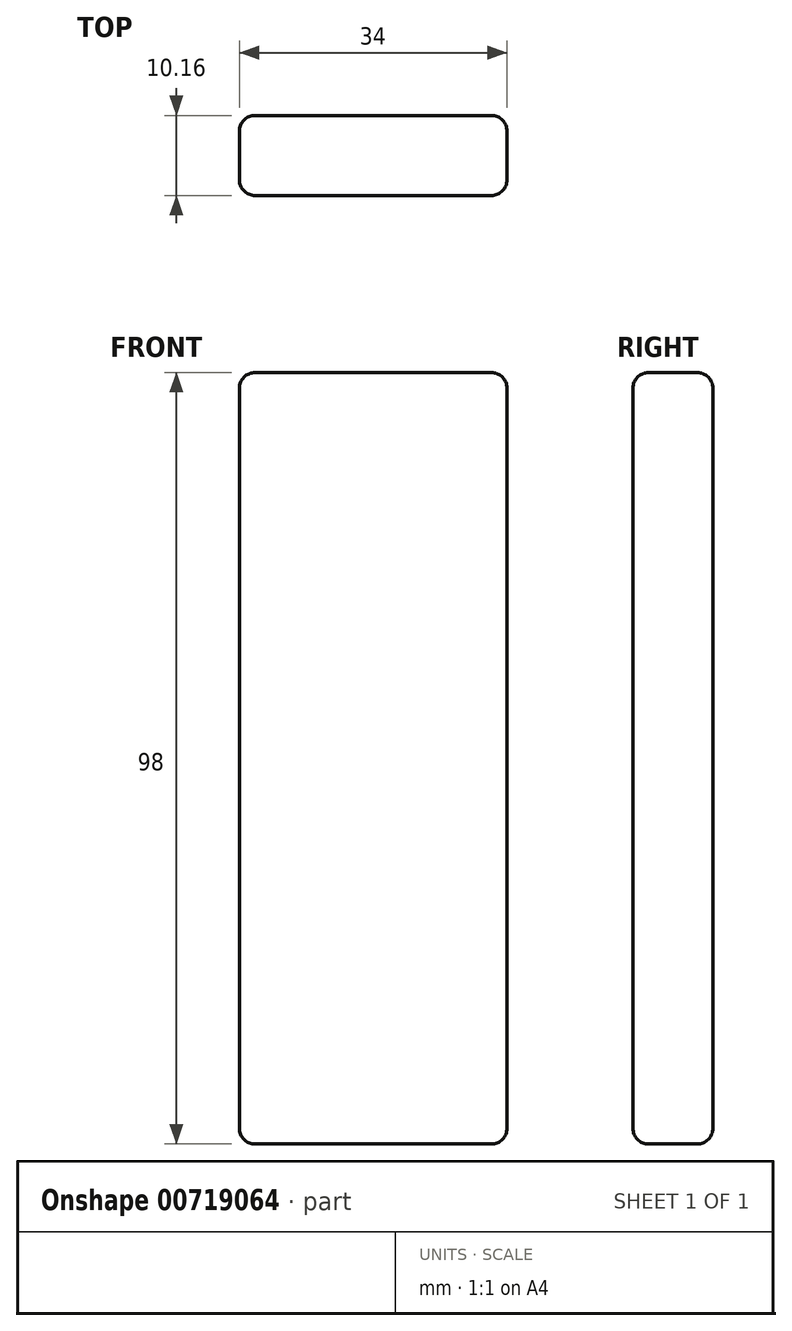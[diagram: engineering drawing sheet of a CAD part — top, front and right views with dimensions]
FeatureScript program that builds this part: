
annotation { "Feature Type Name" : "Feature", "Feature Type Description" : "" }
export const myFeature = defineFeature(function(context is Context, id is Id, definition is map)
    precondition{}
    {
        {
            var Q0;
            Q0=qCreatedBy(makeId("Front.planeOp"),FACE);
            var sketch = newSketch(context, id + "F0", { "sketchPlane" : qUnion([Q0])});
            skLineSegment(sketch, "E0.bottom", {"start": v(-17, 55.23) * mm, "end": v(17, 55.23) * mm});
            skLineSegment(sketch, "E0.top", {"start": v(-17, -42.77) * mm, "end": v(17, -42.77) * mm});
            skLineSegment(sketch, "E0.left", {"start": v(-17, 55.23) * mm, "end": v(-17, -42.77) * mm});
            skLineSegment(sketch, "E0.right", {"start": v(17, 55.23) * mm, "end": v(17, -42.77) * mm});
            skSolve(sketch);
        }
        {
            var Q0;
            Q0=makeQuery(id+"F0.imprint","IMPRINT",FACE,{"disambiguationData":[TD([[makeQuery(id+"F0.imprint","IMPRINT",EDGE,{"derivedFrom":sQuery(id+"F0.wireOp",EDGE,"E0.bottom")}),-1.0]])]});
            extrude(context, id + "F1", {"entities" : qUnion([Q0]), "endBound" : BoundingType.SYMMETRIC, "depth" : 10.16 * mm, "offsetDistance" : 25.4 * mm});
        }
        {
            var Q0;
            Q0=makeQuery(id+"F1.opExtrude","SWEPT_EDGE",EDGE,{"disambiguationData":[OSD([sQuery(id+"F0.wireOp",EDGE,"E0.top"),sQuery(id+"F0.wireOp",EDGE,"E0.right")])]});
            var Q1;
            Q1=makeQuery(id+"F1.opExtrude","CAP_FACE",FACE,{"disambiguationData":[OSD([sQuery(id+"F0.wireOp",EDGE,"E0.bottom"),sQuery(id+"F0.wireOp",EDGE,"E0.top"),sQuery(id+"F0.wireOp",EDGE,"E0.left"),sQuery(id+"F0.wireOp",EDGE,"E0.right")])],"isStart":false});
            var Q2;
            Q2=makeQuery(id+"F1.opExtrude","CAP_FACE",FACE,{"disambiguationData":[OSD([sQuery(id+"F0.wireOp",EDGE,"E0.bottom"),sQuery(id+"F0.wireOp",EDGE,"E0.top"),sQuery(id+"F0.wireOp",EDGE,"E0.left"),sQuery(id+"F0.wireOp",EDGE,"E0.right")])],"isStart":true});
            var Q3;
            Q3=makeQuery(id+"F1.opExtrude","SWEPT_EDGE",EDGE,{"disambiguationData":[OSD([sQuery(id+"F0.wireOp",EDGE,"E0.bottom"),sQuery(id+"F0.wireOp",EDGE,"E0.right")])]});
            var Q4;
            Q4=makeQuery(id+"F1.opExtrude","SWEPT_FACE",FACE,{"disambiguationData":[OSD([sQuery(id+"F0.wireOp",EDGE,"E0.bottom")])]});
            var Q5;
            Q5=makeQuery(id+"F1.opExtrude","SWEPT_EDGE",EDGE,{"disambiguationData":[OSD([sQuery(id+"F0.wireOp",EDGE,"E0.bottom"),sQuery(id+"F0.wireOp",EDGE,"E0.left")])]});
            var Q6;
            Q6=makeQuery(id+"F1.opExtrude","SWEPT_FACE",FACE,{"disambiguationData":[OSD([sQuery(id+"F0.wireOp",EDGE,"E0.top")])]});
            var Q7;
            Q7=makeQuery(id+"F1.opExtrude","CAP_EDGE",EDGE,{"disambiguationData":[OSD([sQuery(id+"F0.wireOp",EDGE,"E0.bottom")])],"isStart":true});
            var Q8;
            Q8=makeQuery(id+"F1.opExtrude","SWEPT_FACE",FACE,{"disambiguationData":[OSD([sQuery(id+"F0.wireOp",EDGE,"E0.left")])]});
            var Q9;
            Q9=makeQuery(id+"F1.opExtrude","CAP_EDGE",EDGE,{"disambiguationData":[OSD([sQuery(id+"F0.wireOp",EDGE,"E0.bottom")])],"isStart":false});
            var Q10;
            Q10=makeQuery(id+"F1.opExtrude","SWEPT_FACE",FACE,{"disambiguationData":[OSD([sQuery(id+"F0.wireOp",EDGE,"E0.right")])]});
            var Q11;
            Q11=makeQuery(id+"F1.opExtrude","CAP_EDGE",EDGE,{"disambiguationData":[OSD([sQuery(id+"F0.wireOp",EDGE,"E0.top")])],"isStart":false});
            var Q12;
            Q12=makeQuery(id+"F1.opExtrude","SWEPT_EDGE",EDGE,{"disambiguationData":[OSD([sQuery(id+"F0.wireOp",EDGE,"E0.top"),sQuery(id+"F0.wireOp",EDGE,"E0.left")])]});
            var Q13;
            Q13=makeQuery(id+"F1.opExtrude","CAP_EDGE",EDGE,{"disambiguationData":[OSD([sQuery(id+"F0.wireOp",EDGE,"E0.top")])],"isStart":true});
            var Q14;
            Q14=makeQuery(id+"F1.opExtrude","CAP_EDGE",EDGE,{"disambiguationData":[OSD([sQuery(id+"F0.wireOp",EDGE,"E0.left")])],"isStart":true});
            var Q15;
            Q15=makeQuery(id+"F1.opExtrude","CAP_EDGE",EDGE,{"disambiguationData":[OSD([sQuery(id+"F0.wireOp",EDGE,"E0.left")])],"isStart":false});
            var Q16;
            Q16=makeQuery(id+"F1.opExtrude","CAP_EDGE",EDGE,{"disambiguationData":[OSD([sQuery(id+"F0.wireOp",EDGE,"E0.right")])],"isStart":true});
            var Q17;
            Q17=makeQuery(id+"F1.opExtrude","CAP_EDGE",EDGE,{"disambiguationData":[OSD([sQuery(id+"F0.wireOp",EDGE,"E0.right")])],"isStart":false});
            fillet(context, id + "F2", {"entities" : qUnion([Q0, Q1, Q2, Q3, Q4, Q5, Q6, Q7, Q8, Q9, Q10, Q11, Q12, Q13, Q14, Q15, Q16, Q17]), "radius" : 2 * mm, "tangentPropagation" : true, "allowEdgeOverflow" : false});
        }
    });
